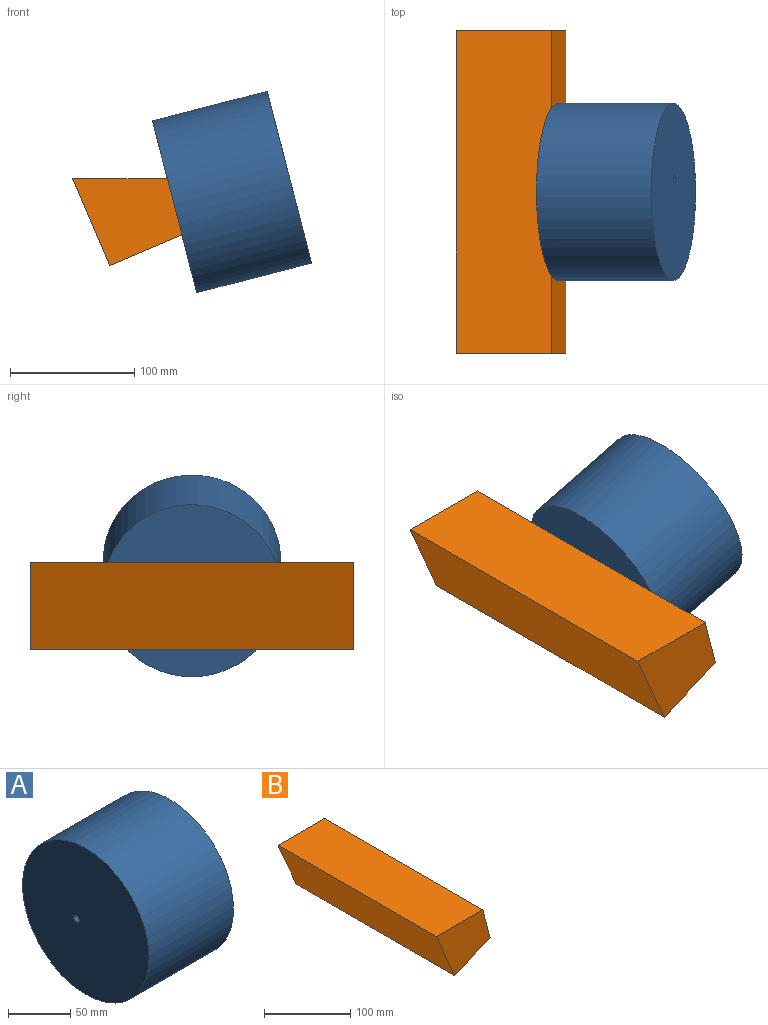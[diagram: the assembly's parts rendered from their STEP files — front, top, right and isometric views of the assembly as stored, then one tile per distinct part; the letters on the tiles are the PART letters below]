
ASSEMBLY  parts=2 mates=1
PART A: 4 faces, bbox 95.5x143.2x143.2 mm
  f0: cylinder r=71.62mm len=143.24mm, axis (-1,0,0), area 42975.7mm2, adj f1,f2
  f1: plane 143.24x143.24mm, normal (1,0,0), area 16081.9mm2, adj f0,f3
  f2: plane 143.24x143.24mm, normal (-1,0,0), area 16081.9mm2, adj f0,f3
  f3: cylinder r=3.17mm len=95.5mm, axis (1,0,0), area 1905.2mm2, adj f1,f2
PART B: 6 faces, bbox 88.3x260x70.4 mm
  f0: plane 260x76.53mm, normal (0,0,1), area 19897.9mm2, adj f1,f3,f4,f5
  f1: plane 260x70.39mm, normal (-0.92,0,-0.39), area 19905.1mm2, adj f0,f2,f4,f5
  f2: plane 260x58.16mm, normal (0.39,0,-0.92), area 16455.4mm2, adj f1,f3,f4,f5
  f3: plane 260x45.44mm, normal (0.97,0,0.25), area 12201.6mm2, adj f0,f2,f4,f5
  f4: plane 88.27x70.39mm, normal (0,-1,0), area 4161.4mm2, adj f0,f1,f2,f3
  f5: plane 88.27x70.39mm, normal (0,1,0), area 4161.4mm2, adj f0,f1,f2,f3
PLACE A rot(axis=(0,-1,0),14.5deg) t=(-196.24,-160.38,-1.41)mm
PLACE B t=(-204.48,165.04,-119.44)mm
MATE parallel A.f2 <-> B.f3  axis (-0.97,0,-0.25) through (-175.91,35.04,-80.14)mm
